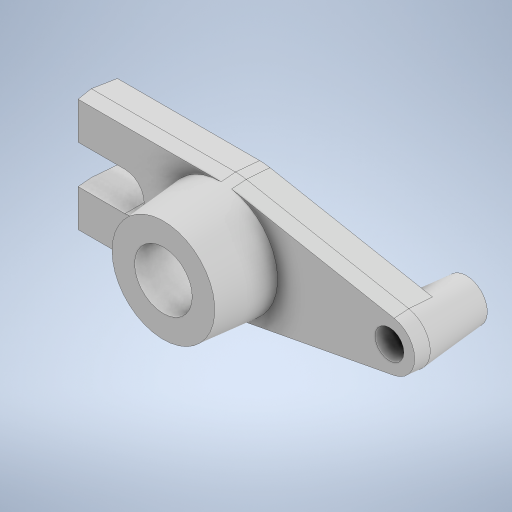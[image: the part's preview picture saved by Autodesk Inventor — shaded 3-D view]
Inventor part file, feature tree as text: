
AUTODESK INVENTOR PART (.ipt)
format: ipt  version: 2023 (Build 270158000, 158)  size: 300,032 bytes
history: native  units: mm
features: extrude x3, other x2, sketch x1
ambient origin geometry x8: Origin, YZ Plane, XZ Plane, XY Plane, X Axis, Y Axis, Z Axis, Center Point
bodies: Solido1 (feature_tree)
feature tree (6):
  sketch  "Schizzo1"
  extrude  "Estrusione1"  Depth=10.0mm
  extrude  "Estrusione2"  Depth=12.0mm
  extrude  "Estrusione3"  Depth=24.0mm
  other  "Sformo faccia1"
  other  "Sformo faccia2"
